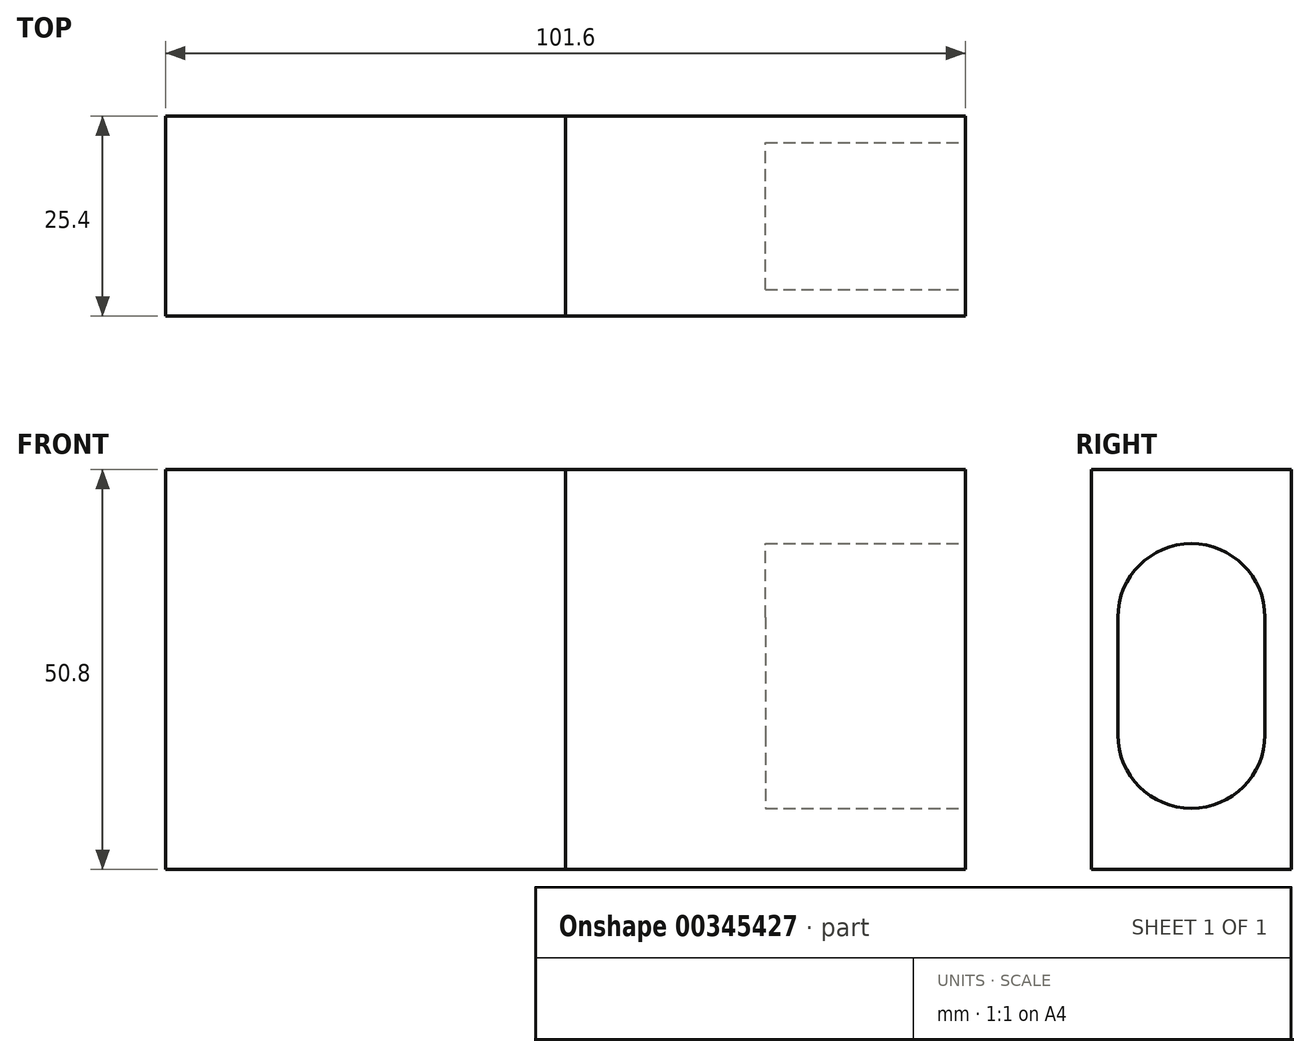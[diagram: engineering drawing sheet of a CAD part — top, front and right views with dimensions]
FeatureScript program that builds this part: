
annotation { "Feature Type Name" : "Feature", "Feature Type Description" : "" }
export const myFeature = defineFeature(function(context is Context, id is Id, definition is map)
    precondition{}
    {
        {
            var Q0;
            Q0=qCreatedBy(makeId("Front.planeOp"),FACE);
            var sketch = newSketch(context, id + "F0", { "sketchPlane" : qUnion([Q0])});
            skLineSegment(sketch, "E0.bottom", {"start": v(0, 0) * mm, "end": v(50.8, 0) * mm});
            skLineSegment(sketch, "E0.top", {"start": v(0, 50.8) * mm, "end": v(50.8, 50.8) * mm});
            skLineSegment(sketch, "E0.left", {"start": v(0, 0) * mm, "end": v(0, 50.8) * mm});
            skLineSegment(sketch, "E0.right", {"start": v(50.8, 0) * mm, "end": v(50.8, 50.8) * mm});
            skSolve(sketch);
        }
        {
            var Q0;
            Q0 = qSketchRegion(id + "F0", true);
            extrude(context, id + "F1", {"entities" : qUnion([Q0]), "endBound" : BoundingType.SYMMETRIC, "depth" : 25.4 * mm, "offsetDistance" : 25.4 * mm});
        }
        {
            var Q0;
            Q0=makeQuery(id+"F1.opExtrude","SWEPT_BODY",BODY,{"disambiguationData":[OSD([sQuery(id+"F0.wireOp",EDGE,"E0.bottom"),sQuery(id+"F0.wireOp",EDGE,"E0.top"),sQuery(id+"F0.wireOp",EDGE,"E0.left"),sQuery(id+"F0.wireOp",EDGE,"E0.right")])]});
            var Q1;
            Q1=qCreatedBy(makeId("Right.planeOp"),FACE);
            mirror(context, id + "F2", {"entities" : qUnion([Q0]), "mirrorPlane" : qUnion([Q1])});
        }
        {
            var Q0;
            Q0=makeQuery(id+"F1.opExtrude","SWEPT_FACE",FACE,{"disambiguationData":[OSD([sQuery(id+"F0.wireOp",EDGE,"E0.right")])]});
            var sketch = newSketch(context, id + "F3", { "sketchPlane" : qUnion([Q0])});
            skLineSegment(sketch, "E1", {"start": v(-9.34, 32.03) * mm, "end": v(-9.34, 17.1) * mm});
            skLineSegment(sketch, "E2", {"start": v(9.34, 32.03) * mm, "end": v(9.34, 17.1) * mm});
            skArc(sketch, "E3", {"start": v(-9.34, 17.1) * mm, "mid": v(0, 7.76) * mm, "end": v(9.34, 17.1) * mm});
            skArc(sketch, "E4", {"start": v(9.34, 32.03) * mm, "mid": v(0, 41.38) * mm, "end": v(-9.34, 32.03) * mm});
            skSolve(sketch);
        }
        {
            var Q0;
            Q0 = qSketchRegion(id + "F3", true);
            extrude(context, id + "F4", {"entities" : qUnion([Q0]), "operationType" : NewBodyOperationType.REMOVE, "oppositeDirection" : true, "depth" : 25.4 * mm, "offsetDistance" : 25.4 * mm});
        }
    });
